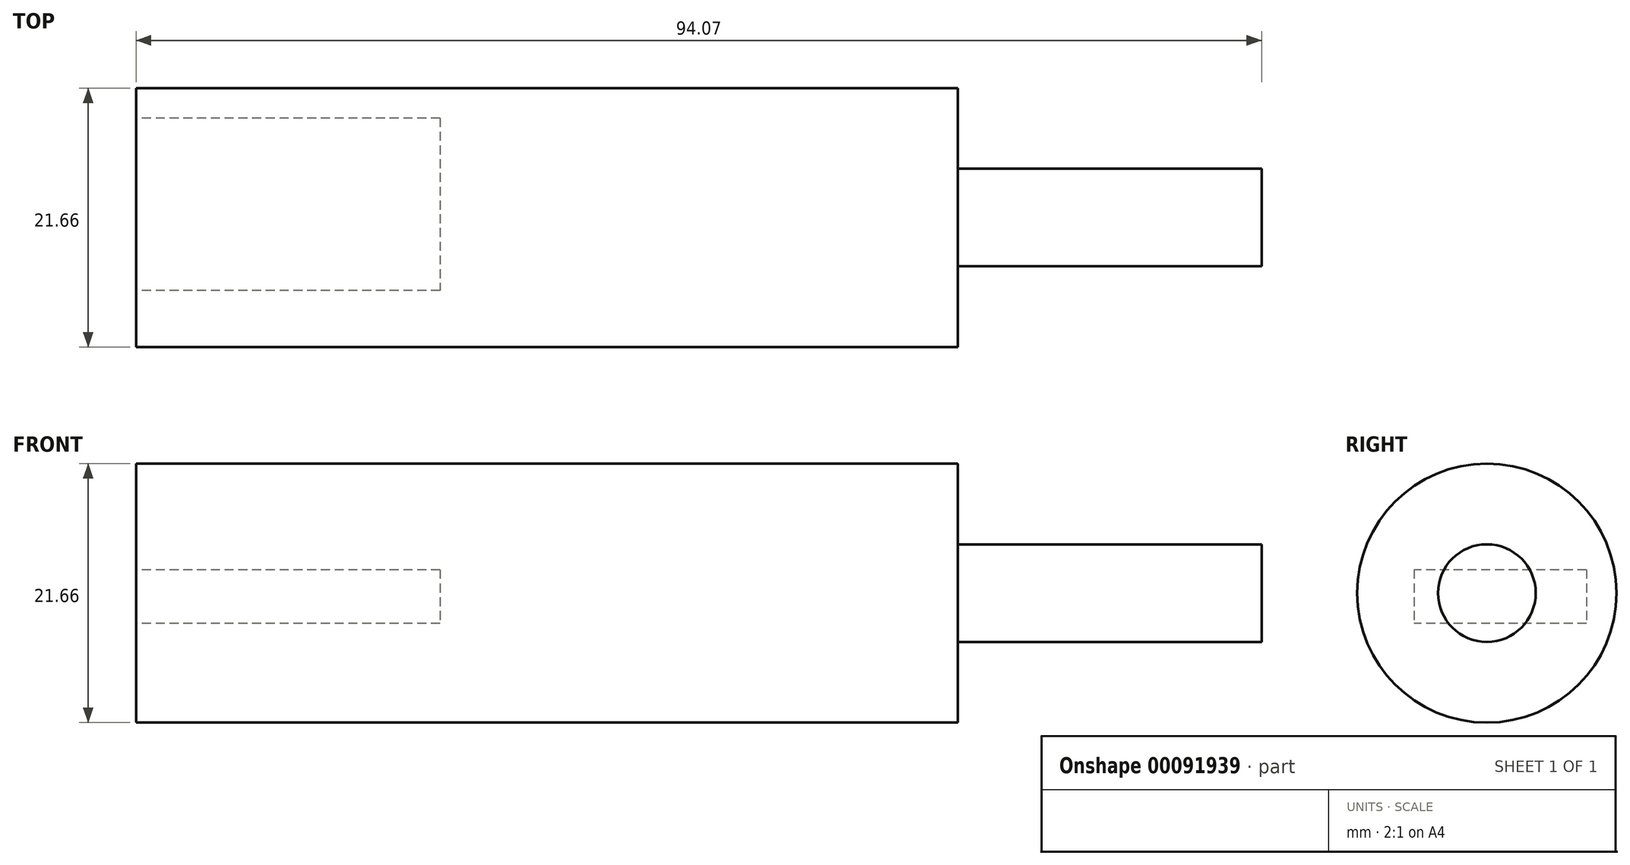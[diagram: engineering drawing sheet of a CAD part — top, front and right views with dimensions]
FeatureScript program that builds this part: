
annotation { "Feature Type Name" : "Feature", "Feature Type Description" : "" }
export const myFeature = defineFeature(function(context is Context, id is Id, definition is map)
    precondition{}
    {
        {
            var Q0;
            Q0=qCreatedBy(makeId("Right.planeOp"),FACE);
            var sketch = newSketch(context, id + "F0", { "sketchPlane" : qUnion([Q0])});
            skCircle(sketch, "E0", {"center": v(0, 0) * mm, "radius": 10.83 * mm});
            skSolve(sketch);
        }
        {
            var Q0;
            Q0 = qSketchRegion(id + "F0", true);
            extrude(context, id + "F1", {"entities" : qUnion([Q0]), "depth" : 68.67 * mm});
        }
        {
            var Q0;
            Q0=makeQuery(id+"F1.opExtrude","CAP_FACE",FACE,{"disambiguationData":[OSD([sQuery(id+"F0.wireOp",EDGE,"E0")])],"isStart":false});
            var sketch = newSketch(context, id + "F2", { "sketchPlane" : qUnion([Q0])});
            skCircle(sketch, "E1", {"center": v(0, 0) * mm, "radius": 4.08 * mm});
            skSolve(sketch);
        }
        {
            var Q0;
            Q0 = qSketchRegion(id + "F2", true);
            extrude(context, id + "F3", {"entities" : qUnion([Q0]), "operationType" : NewBodyOperationType.ADD, "depth" : 25.4 * mm});
        }
        {
            var Q0;
            Q0=makeQuery(id+"F1.opExtrude","CAP_FACE",FACE,{"disambiguationData":[OSD([sQuery(id+"F0.wireOp",EDGE,"E0")])],"isStart":true});
            var sketch = newSketch(context, id + "F4", { "sketchPlane" : qUnion([Q0])});
            skLineSegment(sketch, "E2.bottom", {"start": v(-8.33, 1.95) * mm, "end": v(6.1, 1.95) * mm});
            skLineSegment(sketch, "E2.top", {"start": v(-8.33, -2.53) * mm, "end": v(6.1, -2.53) * mm});
            skLineSegment(sketch, "E2.left", {"start": v(-8.33, 1.95) * mm, "end": v(-8.33, -2.53) * mm});
            skLineSegment(sketch, "E2.right", {"start": v(6.1, 1.95) * mm, "end": v(6.1, -2.53) * mm});
            skSolve(sketch);
        }
        {
            var Q0;
            Q0 = qSketchRegion(id + "F4", true);
            extrude(context, id + "F5", {"entities" : qUnion([Q0]), "operationType" : NewBodyOperationType.REMOVE, "oppositeDirection" : true, "depth" : 25.4 * mm});
        }
    });
